# Revit family: FU_Chair_Sandler_Coco 2-3
name_source: partatom
category: Furniture
units: mm (PartAtom-declared; Revit-internal decimal feet)

## family parameters
Always vertical = Yes
Cut with Voids When Loaded = No
OmniClass Number = 23.40.20.00
OmniClass Title = General Furniture and Specialties
Room Calculation Point = No
Shared = No
Work Plane-Based = No

## types (1)
- Coco 2.3
    Default Elevation = 0 mm  [stored 0 ft]
    Depth = 510 mm  [stored 1.67323 ft]
    Description = Semi-arm chair with solid beech frame and fully upholstered seat and back.
    Frame = Wood - Beech - Walnut - V
    Height = 760 mm
    Manufacturer = Sandler
    Model = Coco 2.3
    Seat = Fabric - Mainline Flax - Bayswater MLF24
    URL = https://www.sandlerseating.com
    Width = 540 mm  [stored 1.77165 ft]

note: [stored X ft] marks values corroborated as IEEE doubles in the binary element streams (Revit-internal decimal feet)

## geometry (parser evidence)
native form markers: Sweep x3
no freeform markers — native parametric forms only
